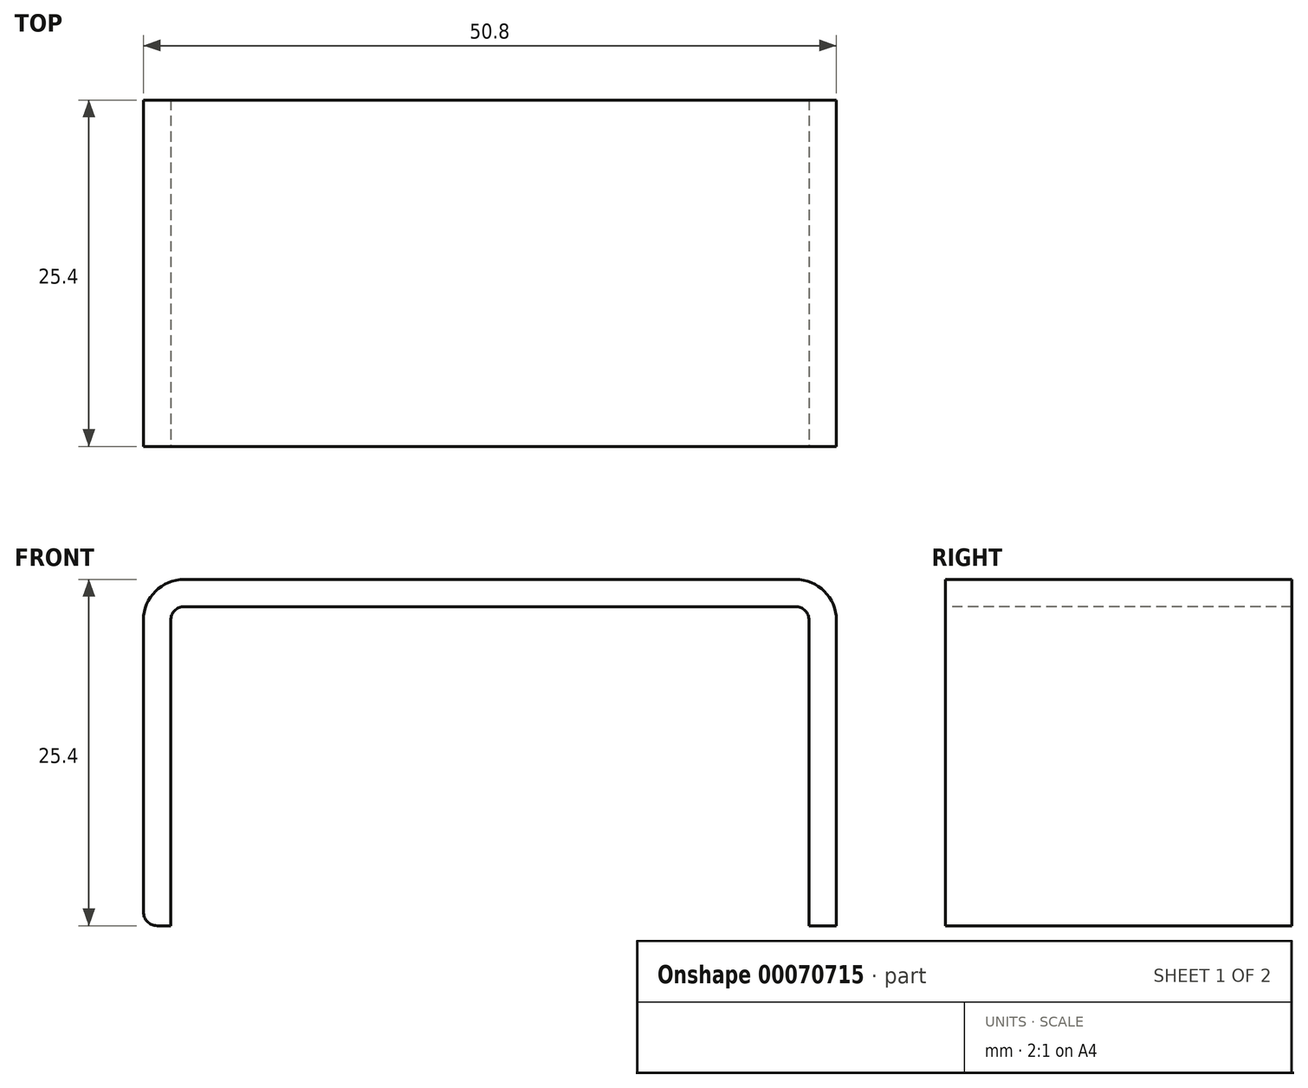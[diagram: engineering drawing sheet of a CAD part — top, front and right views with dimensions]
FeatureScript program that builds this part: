
annotation { "Feature Type Name" : "Feature", "Feature Type Description" : "" }
export const myFeature = defineFeature(function(context is Context, id is Id, definition is map)
    precondition{}
    {
        {
            var Q0;
            Q0=qCreatedBy(makeId("Front.planeOp"),FACE);
            var sketch = newSketch(context, id + "F0", { "sketchPlane" : qUnion([Q0])});
            skLineSegment(sketch, "E0.rect.bottom", {"start": v(-25.4, 12.7) * mm, "end": v(25.4, 12.7) * mm});
            skLineSegment(sketch, "E0.rect.top", {"start": v(-25.4, -12.7) * mm, "end": v(25.4, -12.7) * mm});
            skLineSegment(sketch, "E0.rect.left", {"start": v(-25.4, 12.7) * mm, "end": v(-25.4, -12.7) * mm});
            skLineSegment(sketch, "E0.rect.right", {"start": v(25.4, 12.7) * mm, "end": v(25.4, -12.7) * mm});
            skPoint(sketch, "E0.rect.middle", {"position": v(0, 0) * mm});
            skSolve(sketch);
        }
        {
            var Q0;
            Q0 = qSketchRegion(id + "F0", true);
            extrude(context, id + "F1", {"entities" : qUnion([Q0]), "depth" : 25.4 * mm, "symmetric" : true});
        }
        {
            var Q0;
            Q0=makeQuery(id+"F1.opExtrude","CAP_FACE",FACE,{"disambiguationData":[OSD([sQuery(id+"F0.wireOp",EDGE,"E0.rect.bottom"),sQuery(id+"F0.wireOp",EDGE,"E0.rect.top"),sQuery(id+"F0.wireOp",EDGE,"E0.rect.left"),sQuery(id+"F0.wireOp",EDGE,"E0.rect.right")])],"isStart":false});
            var sketch = newSketch(context, id + "F2", { "sketchPlane" : qUnion([Q0])});
            skLineSegment(sketch, "E1.bottom", {"start": v(-23.4, -12.7) * mm, "end": v(23.4, -12.7) * mm});
            skLineSegment(sketch, "E1.top", {"start": v(-23.4, 10.7) * mm, "end": v(23.4, 10.7) * mm});
            skLineSegment(sketch, "E1.left", {"start": v(-23.4, -12.7) * mm, "end": v(-23.4, 10.7) * mm});
            skLineSegment(sketch, "E1.right", {"start": v(23.4, -12.7) * mm, "end": v(23.4, 10.7) * mm});
            skSolve(sketch);
        }
        {
            var Q0;
            Q0 = qSketchRegion(id + "F2", true);
            var Q1;
            Q1=makeQuery(id+"F1.opExtrude","CAP_FACE",FACE,{"disambiguationData":[OSD([sQuery(id+"F0.wireOp",EDGE,"E0.rect.bottom"),sQuery(id+"F0.wireOp",EDGE,"E0.rect.top"),sQuery(id+"F0.wireOp",EDGE,"E0.rect.left"),sQuery(id+"F0.wireOp",EDGE,"E0.rect.right")])],"isStart":true});
            extrude(context, id + "F3", {"entities" : qUnion([Q0]), "operationType" : NewBodyOperationType.REMOVE, "endBound" : BoundingType.UP_TO_SURFACE, "oppositeDirection" : true, "endBoundEntityFace" : qUnion([Q1]), "depth" : 25 * mm});
        }
        {
            var Q0;
            Q0=makeQuery(id+"F1.opExtrude","SWEPT_EDGE",EDGE,{"disambiguationData":[OSD([sQuery(id+"F0.wireOp",EDGE,"E0.rect.bottom"),sQuery(id+"F0.wireOp",EDGE,"E0.rect.left")])]});
            var Q1;
            Q1=makeQuery(id+"F1.opExtrude","SWEPT_EDGE",EDGE,{"disambiguationData":[OSD([sQuery(id+"F0.wireOp",EDGE,"E0.rect.bottom"),sQuery(id+"F0.wireOp",EDGE,"E0.rect.right")])]});
            fillet(context, id + "F4", {"entities" : qUnion([Q0, Q1]), "radius" : 3 * mm, "tangentPropagation" : true, "allowEdgeOverflow" : false});
        }
        {
            var Q0;
            Q0=makeQuery(id+"F3.boolean.opBoolean","COPY",EDGE,{"derivedFrom":makeQuery(id+"F3.opExtrude","SWEPT_EDGE",EDGE,{"disambiguationData":[OSD([sQuery(id+"F2.wireOp",EDGE,"E1.top"),sQuery(id+"F2.wireOp",EDGE,"E1.left")])]})});
            var Q1;
            Q1=makeQuery(id+"F3.boolean.opBoolean","COPY",EDGE,{"derivedFrom":makeQuery(id+"F3.opExtrude","SWEPT_EDGE",EDGE,{"disambiguationData":[OSD([sQuery(id+"F2.wireOp",EDGE,"E1.top"),sQuery(id+"F2.wireOp",EDGE,"E1.right")])]})});
            fillet(context, id + "F5", {"entities" : qUnion([Q0, Q1]), "radius" : 1 * mm, "tangentPropagation" : true, "allowEdgeOverflow" : false});
        }
        {
            var Q0;
            Q0=makeQuery(id+"F1.opExtrude","SWEPT_EDGE",EDGE,{"disambiguationData":[OSD([sQuery(id+"F0.wireOp",EDGE,"E0.rect.top"),sQuery(id+"F0.wireOp",EDGE,"E0.rect.left")])]});
            var Q1;
            Q1=makeQuery(id+"F3.boolean.opBoolean","COPY",EDGE,{"derivedFrom":makeQuery(id+"F3.opExtrude","SWEPT_EDGE",EDGE,{"disambiguationData":[OSD([sQuery(id+"F0.wireOp",EDGE,"E0.rect.top"),sQuery(id+"F2.wireOp",EDGE,"E1.bottom"),sQuery(id+"F2.wireOp",EDGE,"E1.left")])]})});
            fillet(context, id + "F6", {"entities" : qUnion([Q0, Q1]), "radius" : 1 * mm, "tangentPropagation" : true, "allowEdgeOverflow" : false});
        }
    });
